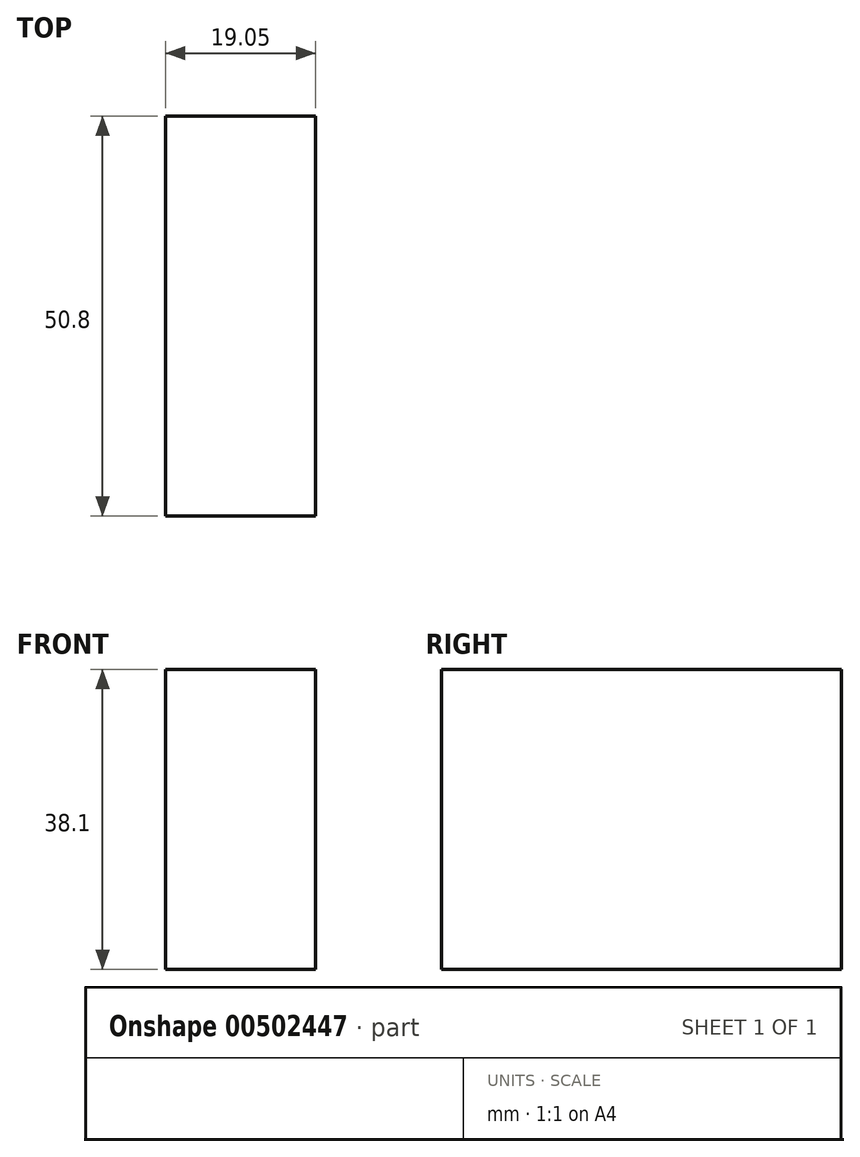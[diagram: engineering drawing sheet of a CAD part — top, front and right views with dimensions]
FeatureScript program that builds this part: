
annotation { "Feature Type Name" : "Feature", "Feature Type Description" : "" }
export const myFeature = defineFeature(function(context is Context, id is Id, definition is map)
    precondition{}
    {
        {
            var Q0;
            Q0=qCreatedBy(makeId("Front.planeOp"),FACE);
            var sketch = newSketch(context, id + "F0", { "sketchPlane" : qUnion([Q0])});
            skLineSegment(sketch, "E0.bottom", {"start": v(0, 38.1) * mm, "end": v(19.05, 38.1) * mm});
            skLineSegment(sketch, "E0.top", {"start": v(0, 0) * mm, "end": v(19.05, 0) * mm});
            skLineSegment(sketch, "E0.left", {"start": v(0, 38.1) * mm, "end": v(0, 0) * mm});
            skLineSegment(sketch, "E0.right", {"start": v(19.05, 38.1) * mm, "end": v(19.05, 0) * mm});
            skSolve(sketch);
        }
        {
            var Q0;
            Q0=makeQuery(id+"F0.imprint","IMPRINT",FACE,{"disambiguationData":[TD([[makeQuery(id+"F0.imprint","IMPRINT",EDGE,{"derivedFrom":sQuery(id+"F0.wireOp",EDGE,"E0.bottom")}),-1.0]])]});
            extrude(context, id + "F1", {"entities" : qUnion([Q0]), "depth" : 50.8 * mm});
        }
    });
